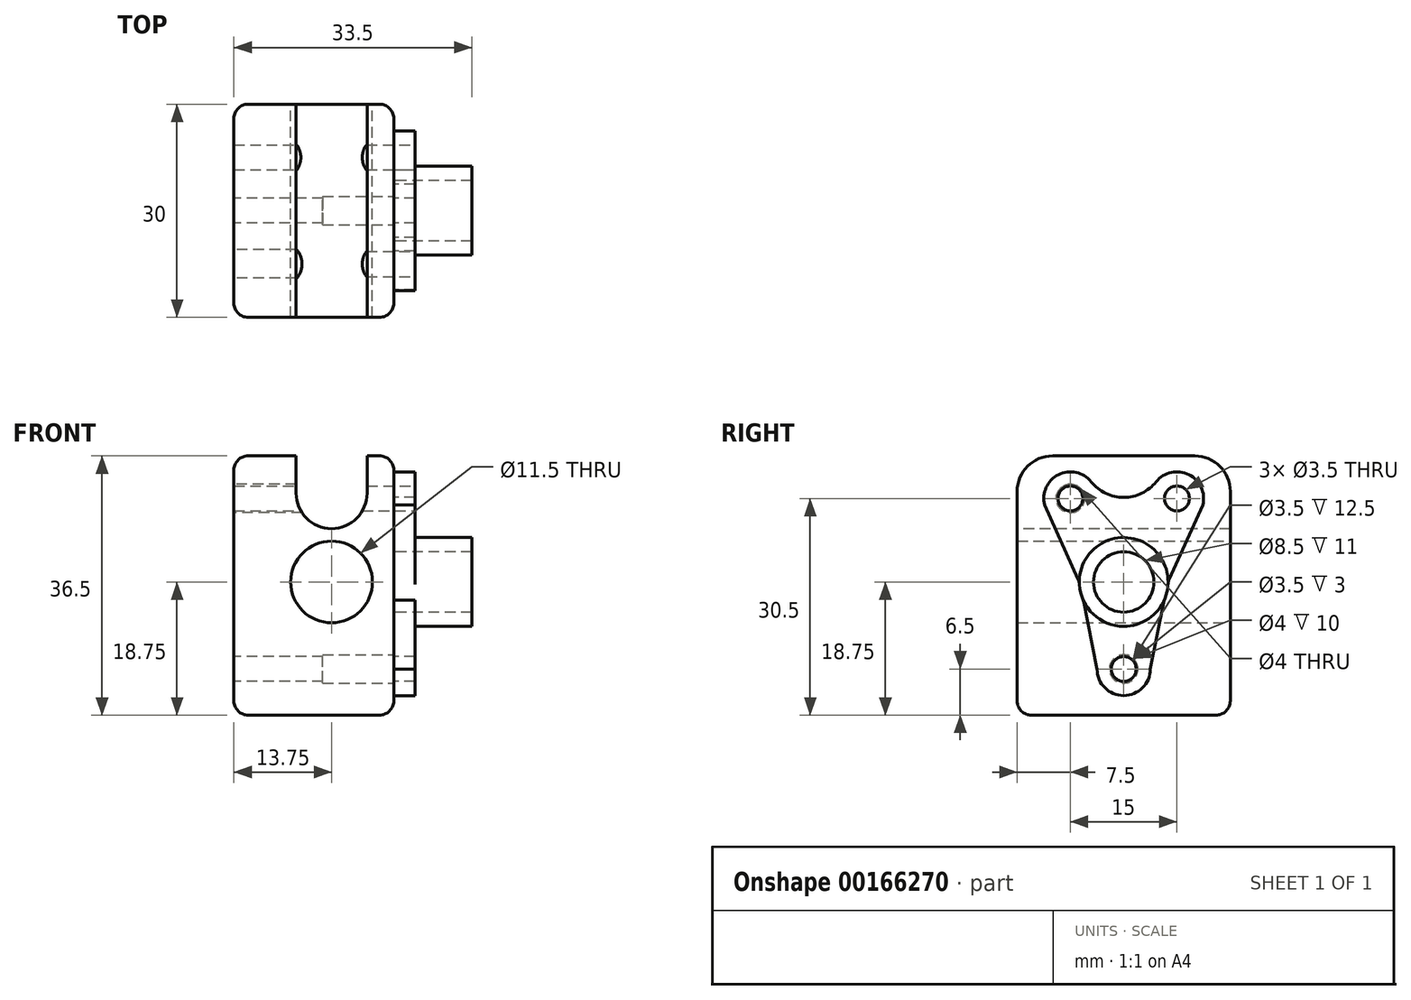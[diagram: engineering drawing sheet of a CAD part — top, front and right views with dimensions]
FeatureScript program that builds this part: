
annotation { "Feature Type Name" : "Feature", "Feature Type Description" : "" }
export const myFeature = defineFeature(function(context is Context, id is Id, definition is map)
    precondition{}
    {
        {
            var Q0;
            Q0=qCreatedBy(makeId("Front.planeOp"),FACE);
            var sketch = newSketch(context, id + "F0", { "sketchPlane" : qUnion([Q0])});
            skCircle(sketch, "E0", {"center": v(0, 0) * mm, "radius": 5.75 * mm});
            skLineSegment(sketch, "E1.bottom", {"start": v(-13.75, 17.75) * mm, "end": v(8.75, 17.75) * mm});
            skLineSegment(sketch, "E1.left", {"start": v(-13.75, 17.75) * mm, "end": v(-13.75, -8.75) * mm});
            skLineSegment(sketch, "E1.right", {"start": v(8.75, 17.75) * mm, "end": v(8.75, -8.75) * mm});
            skLineSegment(sketch, "E2", {"start": v(0, 0) * mm, "end": v(0, 17.75) * mm, "construction": true});
            skLineSegment(sketch, "E3", {"start": v(8.75, -8.75) * mm, "end": v(-5.75, -8.75) * mm});
            skLineSegment(sketch, "E4", {"start": v(-13.75, -16) * mm, "end": v(-5.75, -16) * mm, "construction": true});
            skLineSegment(sketch, "E5", {"start": v(-13.75, -16) * mm, "end": v(-13.75, -23.25) * mm, "construction": true});
            skLineSegment(sketch, "E6", {"start": v(-13.75, -23.25) * mm, "end": v(-5.75, -23.25) * mm, "construction": true});
            skLineSegment(sketch, "E7", {"start": v(-5.75, -23.25) * mm, "end": v(-5.75, -16) * mm, "construction": true});
            skLineSegment(sketch, "E8", {"start": v(-5.75, -16) * mm, "end": v(-5.75, -8.75) * mm, "construction": true});
            skCircle(sketch, "E9", {"center": v(-5.75, -16) * mm, "radius": 2.5 * mm, "construction": true});
            skLineSegment(sketch, "E10", {"start": v(-5.75, -8.75) * mm, "end": v(-5.75, 0) * mm, "construction": true});
            skLineSegment(sketch, "E11", {"start": v(-5.75, -23.25) * mm, "end": v(8.75, -23.25) * mm, "construction": true});
            skLineSegment(sketch, "E12", {"start": v(8.75, -23.25) * mm, "end": v(8.75, -8.75) * mm, "construction": true});
            skLineSegment(sketch, "E13", {"start": v(-5.75, -8.75) * mm, "end": v(-13.75, -8.75) * mm});
            skSolve(sketch);
        }
        {
            var Q0;
            Q0=qSketchRegion(id+"F0",true);
            extrude(context, id + "F1", {"entities" : qUnion([Q0]), "depth" : 30 * mm});
        }
        {
            var Q0;
            {var subQ0=sQuery(id+"F0.wireOp",EDGE,"E1.right");Q0=makeQuery(id+"FleU8CKk3SzImxh_1.boolean.opBoolean","MERGE",FACE,{"derivedFrom":[makeQuery(id+"F1.opExtrude","SWEPT_FACE",FACE,{"disambiguationData":[OSD([subQ0])]}),makeQuery(id+"FleU8CKk3SzImxh_1.opExtrude","CAP_FACE",FACE,{"disambiguationData":[OSD([subQ0])],"isStart":false})]});}
            var sketch = newSketch(context, id + "F2", { "sketchPlane" : qUnion([Q0])});
            skLineSegment(sketch, "E14", {"start": v(0, -5.75) * mm, "end": v(-30, -5.75) * mm, "construction": true});
            skLineSegment(sketch, "E15", {"start": v(-30, 5.75) * mm, "end": v(0, 5.75) * mm, "construction": true});
            skLineSegment(sketch, "E16", {"start": v(-15, -5.75) * mm, "end": v(-15, 5.75) * mm, "construction": true});
            skCircle(sketch, "E17", {"center": v(-15, 0) * mm, "radius": 4.25 * mm});
            skArc(sketch, "E18.0", {"start": v(-21.25, 0) * mm, "mid": v(-15, -6.25) * mm, "end": v(-8.75, 0) * mm});
            skLineSegment(sketch, "E19", {"start": v(-15, 5.75) * mm, "end": v(-15, 17.75) * mm, "construction": true});
            skCircle(sketch, "E20", {"center": v(-22.5, 11.75) * mm, "radius": 1.75 * mm});
            skPoint(sketch, "E20.centerSnap0", {"position": v(-15, 11.75) * mm});
            skCircle(sketch, "E21.MirrorC", {"center": v(-7.5, 11.75) * mm, "radius": 1.75 * mm});
            skLineSegment(sketch, "E22", {"start": v(-30, 17.75) * mm, "end": v(-15, 17.75) * mm, "construction": true});
            skPoint(sketch, "E23", {"position": v(-22.5, 17.75) * mm});
            skArc(sketch, "E24.0", {"start": v(-19.57, 14.1) * mm, "mid": v(-24.72, 14.77) * mm, "end": v(-25.6, 9.65) * mm});
            skArc(sketch, "E25.MirrorC", {"start": v(-10.43, 14.1) * mm, "mid": v(-5.82, 15.1) * mm, "end": v(-3.87, 10.81) * mm});
            skLineSegment(sketch, "E26", {"start": v(-3.87, 10.81) * mm, "end": v(-8.75, 0) * mm});
            skArc(sketch, "E27", {"start": v(-19.57, 14.1) * mm, "mid": v(-15, 11.9) * mm, "end": v(-10.43, 14.1) * mm});
            skLineSegment(sketch, "E28.MirrorCS", {"start": v(-26.13, 10.81) * mm, "end": v(-21.25, 0) * mm});
            skSolve(sketch);
        }
        {
            var Q0;
            Q0=makeQuery(id+"F2.imprint","IMPRINT",FACE,{"disambiguationData":[TD([[makeQuery(id+"F2.imprint","IMPRINT",EDGE,{"derivedFrom":sQuery(id+"F2.wireOp",EDGE,"E17")}),-1.0]])]});
            extrude(context, id + "F3", {"entities" : qUnion([Q0]), "depth" : 3 * mm});
        }
        {
            var Q0;
            Q0=makeQuery(id+"F3.opExtrude","CAP_FACE",FACE,{"disambiguationData":[OSD([sQuery(id+"F2.wireOp",EDGE,"E17"),sQuery(id+"F2.wireOp",EDGE,"E18.0"),sQuery(id+"F2.wireOp",EDGE,"E20"),sQuery(id+"F2.wireOp",EDGE,"E21.MirrorC"),sQuery(id+"F2.wireOp",EDGE,"E24.0"),sQuery(id+"F2.wireOp",EDGE,"E25.MirrorC"),sQuery(id+"F2.wireOp",EDGE,"E26"),sQuery(id+"F2.wireOp",EDGE,"E27"),sQuery(id+"F2.wireOp",EDGE,"E28.MirrorCS")])],"isStart":false});
            var sketch = newSketch(context, id + "F4", { "sketchPlane" : qUnion([Q0])});
            skCircle(sketch, "E29.0", {"center": v(-15, 0) * mm, "radius": 4.25 * mm});
            skCircle(sketch, "E30", {"center": v(-15, 0) * mm, "radius": 6.25 * mm});
            skSolve(sketch);
        }
        {
            var Q0;
            Q0=makeQuery(id+"F4.imprint","IMPRINT",FACE,{"disambiguationData":[TD([[makeQuery(id+"F4.imprint","IMPRINT",EDGE,{"derivedFrom":sQuery(id+"F4.wireOp",EDGE,"E29.0")}),-1.0]])]});
            extrude(context, id + "F5", {"entities" : qUnion([Q0]), "operationType" : NewBodyOperationType.ADD, "depth" : 8 * mm});
        }
        {
            var Q0;
            {var subQ0=sQuery(id+"F0.wireOp",EDGE,"E1.right");Q0=makeQuery(id+"FleU8CKk3SzImxh_1.boolean.opBoolean","MERGE",FACE,{"derivedFrom":[makeQuery(id+"F1.opExtrude","SWEPT_FACE",FACE,{"disambiguationData":[OSD([subQ0])]}),makeQuery(id+"FleU8CKk3SzImxh_1.opExtrude","CAP_FACE",FACE,{"disambiguationData":[OSD([subQ0])],"isStart":false})]});}
            var sketch = newSketch(context, id + "F6", { "sketchPlane" : qUnion([Q0])});
            skCircle(sketch, "E31.0", {"center": v(-22.5, 11.75) * mm, "radius": 1.75 * mm});
            skCircle(sketch, "E32.0", {"center": v(-7.5, 11.75) * mm, "radius": 1.75 * mm});
            skSolve(sketch);
        }
        {
            var Q0;
            Q0=makeQuery(id+"F6.imprint","IMPRINT",FACE,{"disambiguationData":[TD([[makeQuery(id+"F6.imprint","IMPRINT",EDGE,{"derivedFrom":sQuery(id+"F6.wireOp",EDGE,"E31.0")}),1.0]])]});
            var Q1;
            Q1=makeQuery(id+"F6.imprint","IMPRINT",FACE,{"disambiguationData":[TD([[makeQuery(id+"F6.imprint","IMPRINT",EDGE,{"derivedFrom":sQuery(id+"F6.wireOp",EDGE,"E32.0")}),1.0]])]});
            extrude(context, id + "F7", {"entities" : qUnion([Q0, Q1]), "operationType" : NewBodyOperationType.REMOVE, "endBound" : BoundingType.THROUGH_ALL, "oppositeDirection" : true, "depth" : 25 * mm});
        }
        {
            var Q0;
            Q0=makeQuery(id+"F1.opExtrude","CAP_FACE",FACE,{"disambiguationData":[OSD([sQuery(id+"F0.wireOp",EDGE,"E0"),sQuery(id+"F0.wireOp",EDGE,"E1.bottom"),sQuery(id+"F0.wireOp",EDGE,"E1.left"),sQuery(id+"F0.wireOp",EDGE,"E1.right"),sQuery(id+"F0.wireOp",EDGE,"E5"),sQuery(id+"F0.wireOp",EDGE,"E6"),sQuery(id+"F0.wireOp",EDGE,"E11"),sQuery(id+"F0.wireOp",EDGE,"E12")])],"isStart":true});
            var sketch = newSketch(context, id + "F8", { "sketchPlane" : qUnion([Q0])});
            skLineSegment(sketch, "E33", {"start": v(-8.57, 13.5) * mm, "end": v(11.58, 13.5) * mm, "construction": true});
            skLineSegment(sketch, "E34", {"start": v(11.58, 10) * mm, "end": v(-8.57, 10) * mm, "construction": true});
            skCircle(sketch, "E35.0", {"center": v(0, 0) * mm, "radius": 5.75 * mm, "construction": true});
            skLineSegment(sketch, "E36", {"start": v(0, 0) * mm, "end": v(0, 17.75) * mm, "construction": true});
            skLineSegment(sketch, "E37", {"start": v(5, 10) * mm, "end": v(5, 13.5) * mm, "construction": true});
            skLineSegment(sketch, "E38", {"start": v(0, 7.5) * mm, "end": v(5, 7.5) * mm});
            skLineSegment(sketch, "E39", {"start": v(5, 7.5) * mm, "end": v(5, 17.75) * mm});
            skLineSegment(sketch, "E40.MirrorCS", {"start": v(0, 7.5) * mm, "end": v(-5, 7.5) * mm});
            skLineSegment(sketch, "E41.MirrorCS", {"start": v(-5, 7.5) * mm, "end": v(-5, 17.75) * mm});
            skLineSegment(sketch, "E42", {"start": v(-5, 17.75) * mm, "end": v(5, 17.75) * mm});
            skSolve(sketch);
        }
        {
            var Q0;
            Q0=makeQuery(id+"F8.imprint","IMPRINT",FACE,{"disambiguationData":[TD([[makeQuery(id+"F8.imprint","IMPRINT",EDGE,{"derivedFrom":sQuery(id+"F8.wireOp",EDGE,"E38")}),1.0]])]});
            extrude(context, id + "F9", {"entities" : qUnion([Q0]), "operationType" : NewBodyOperationType.REMOVE, "endBound" : BoundingType.THROUGH_ALL, "oppositeDirection" : true, "depth" : 25 * mm});
        }
        {
            var Q0;
            {var subQ1=sQuery(id+"F0.wireOp",EDGE,"E1.bottom");Q0=makeQuery(id+"F9.boolean.opBoolean","SPLIT",EDGE,{"disambiguationData":[TD([makeQuery(id+"F9.opExtrude","SWEPT_FACE",FACE,{"disambiguationData":[OSD([sQuery(id+"F8.wireOp",EDGE,"E39")])]})])],"derivedFrom":makeQuery(id+"F1.opExtrude","CAP_EDGE",EDGE,{"disambiguationData":[OSD([subQ1])],"isStart":true})});}
            var Q1;
            {var subQ2=sQuery(id+"F0.wireOp",EDGE,"E1.bottom");Q1=makeQuery(id+"F9.boolean.opBoolean","SPLIT",EDGE,{"disambiguationData":[TD([makeQuery(id+"F9.opExtrude","SWEPT_FACE",FACE,{"disambiguationData":[OSD([sQuery(id+"F8.wireOp",EDGE,"E41.MirrorCS")])]})])],"derivedFrom":makeQuery(id+"F1.opExtrude","CAP_EDGE",EDGE,{"disambiguationData":[OSD([subQ2])],"isStart":true})});}
            var Q2;
            Q2=makeQuery(id+"F9.boolean.opBoolean","COPY",EDGE,{"derivedFrom":makeQuery(id+"F9.opExtrude","SWEPT_EDGE",EDGE,{"disambiguationData":[OSD([sQuery(id+"F8.wireOp",EDGE,"E38"),sQuery(id+"F8.wireOp",EDGE,"E39")])]})});
            var Q3;
            {var subQ2=sQuery(id+"F0.wireOp",EDGE,"E1.bottom");Q3=makeQuery(id+"F9.boolean.opBoolean","SPLIT",EDGE,{"disambiguationData":[TD([makeQuery(id+"F9.opExtrude","SWEPT_FACE",FACE,{"disambiguationData":[OSD([sQuery(id+"F8.wireOp",EDGE,"E39")])]})])],"derivedFrom":makeQuery(id+"F1.opExtrude","CAP_EDGE",EDGE,{"disambiguationData":[OSD([subQ2])],"isStart":false})});}
            var Q4;
            Q4=makeQuery(id+"F9.boolean.opBoolean","COPY",EDGE,{"derivedFrom":makeQuery(id+"F9.opExtrude","SWEPT_EDGE",EDGE,{"disambiguationData":[OSD([sQuery(id+"F8.wireOp",EDGE,"E40.MirrorCS"),sQuery(id+"F8.wireOp",EDGE,"E41.MirrorCS")])]})});
            var Q5;
            {var subQ1=sQuery(id+"F0.wireOp",EDGE,"E1.bottom");Q5=makeQuery(id+"F9.boolean.opBoolean","SPLIT",EDGE,{"disambiguationData":[TD([makeQuery(id+"F9.opExtrude","SWEPT_FACE",FACE,{"disambiguationData":[OSD([sQuery(id+"F8.wireOp",EDGE,"E41.MirrorCS")])]})])],"derivedFrom":makeQuery(id+"F1.opExtrude","CAP_EDGE",EDGE,{"disambiguationData":[OSD([subQ1])],"isStart":false})});}
            fillet(context, id + "F10", {"entities" : qUnion([Q0, Q1, Q2, Q3, Q4, Q5]), "radius" : 5 * mm, "tangentPropagation" : true, "allowEdgeOverflow" : false});
        }
        {
            var Q0;
            Q0=makeQuery(id+"F3.opExtrude","CAP_FACE",FACE,{"disambiguationData":[OSD([sQuery(id+"F2.wireOp",EDGE,"E17"),sQuery(id+"F2.wireOp",EDGE,"E18.0"),sQuery(id+"F2.wireOp",EDGE,"E20"),sQuery(id+"F2.wireOp",EDGE,"E21.MirrorC"),sQuery(id+"F2.wireOp",EDGE,"E24.0"),sQuery(id+"F2.wireOp",EDGE,"E25.MirrorC"),sQuery(id+"F2.wireOp",EDGE,"E26"),sQuery(id+"F2.wireOp",EDGE,"E27"),sQuery(id+"F2.wireOp",EDGE,"E28.MirrorCS")])],"isStart":true});
            var sketch = newSketch(context, id + "F11", { "sketchPlane" : qUnion([Q0])});
            skCircle(sketch, "E43.0", {"center": v(15, 0) * mm, "radius": 4.25 * mm});
            skLineSegment(sketch, "E44", {"start": v(15, 0) * mm, "end": v(15, -12.25) * mm, "construction": true});
            skCircle(sketch, "E45", {"center": v(15, -12.25) * mm, "radius": 1.75 * mm});
            skCircle(sketch, "E46.0", {"center": v(15, -12.25) * mm, "radius": 3.75 * mm});
            skLineSegment(sketch, "E47", {"start": v(11.25, -12.25) * mm, "end": v(9.3, -2.58) * mm});
            skLineSegment(sketch, "E48.MirrorCS", {"start": v(18.75, -12.25) * mm, "end": v(20.7, -2.58) * mm});
            skSolve(sketch);
        }
        {
            var Q0;
            {var subQ0=sQuery(id+"F11.wireOp",EDGE,"E47");Q0=makeQuery(id+"F11.imprint","IMPRINT",FACE,{"disambiguationData":[TD([[makeQuery(id+"F11.imprint","IMPRINT",EDGE,{"derivedFrom":subQ0}),-1.0]])]});}
            var Q1;
            Q1=makeQuery(id+"F11.imprint","IMPRINT",FACE,{"disambiguationData":[TD([[makeQuery(id+"F11.imprint","IMPRINT",EDGE,{"derivedFrom":sQuery(id+"F11.wireOp",EDGE,"E45")}),-1.0]])]});
            var Q2;
            Q2=makeQuery(id+"F3.opExtrude","CAP_FACE",FACE,{"disambiguationData":[OSD([sQuery(id+"F2.wireOp",EDGE,"E17"),sQuery(id+"F2.wireOp",EDGE,"E18.0"),sQuery(id+"F2.wireOp",EDGE,"E20"),sQuery(id+"F2.wireOp",EDGE,"E21.MirrorC"),sQuery(id+"F2.wireOp",EDGE,"E24.0"),sQuery(id+"F2.wireOp",EDGE,"E25.MirrorC"),sQuery(id+"F2.wireOp",EDGE,"E26"),sQuery(id+"F2.wireOp",EDGE,"E27"),sQuery(id+"F2.wireOp",EDGE,"E28.MirrorCS")])],"isStart":false});
            extrude(context, id + "F12", {"entities" : qUnion([Q0, Q1]), "operationType" : NewBodyOperationType.ADD, "endBound" : BoundingType.UP_TO_SURFACE, "oppositeDirection" : true, "endBoundEntityFace" : qUnion([Q2]), "depth" : 25 * mm});
        }
        {
            var Q0;
            Q0=makeQuery(id+"F1.opExtrude","SWEPT_FACE",FACE,{"disambiguationData":[OSD([sQuery(id+"F0.wireOp",EDGE,"E3"),sQuery(id+"F0.wireOp",EDGE,"E13")])]});
            extrude(context, id + "F13", {"entities" : qUnion([Q0]), "operationType" : NewBodyOperationType.ADD, "depth" : 10 * mm});
        }
        {
            var Q0;
            Q0=makeQuery(id+"F1.opExtrude","SWEPT_EDGE",EDGE,{"disambiguationData":[OSD([sQuery(id+"F0.wireOp",EDGE,"E1.bottom"),sQuery(id+"F0.wireOp",EDGE,"E1.right")])]});
            var Q1;
            Q1=makeQuery(id+"F1.opExtrude","CAP_EDGE",EDGE,{"disambiguationData":[OSD([sQuery(id+"F0.wireOp",EDGE,"E1.right"),sQuery(id+"F0.wireOp",EDGE,"E12")])],"isStart":false});
            var Q2;
            Q2=makeQuery(id+"F1.opExtrude","CAP_EDGE",EDGE,{"disambiguationData":[OSD([sQuery(id+"F0.wireOp",EDGE,"E1.right"),sQuery(id+"F0.wireOp",EDGE,"E12")])],"isStart":true});
            var Q3;
            Q3=makeQuery(id+"F5.opExtrude","CAP_EDGE",EDGE,{"disambiguationData":[OSD([sQuery(id+"F4.wireOp",EDGE,"E30")])],"isStart":true});
            var Q4;
            Q4=makeQuery(id+"F3.opExtrude","SWEPT_EDGE",EDGE,{"disambiguationData":[OSD([sQuery(id+"F2.wireOp",EDGE,"E18.0"),sQuery(id+"F2.wireOp",EDGE,"E28.MirrorCS")])]});
            var Q5;
            Q5=makeQuery(id+"F3.opExtrude","SWEPT_EDGE",EDGE,{"disambiguationData":[OSD([sQuery(id+"F2.wireOp",EDGE,"E18.0"),sQuery(id+"F2.wireOp",EDGE,"E26")])]});
            var Q6;
            Q6=makeQuery(id+"F1.opExtrude","SWEPT_EDGE",EDGE,{"disambiguationData":[OSD([sQuery(id+"F0.wireOp",EDGE,"E5"),sQuery(id+"F0.wireOp",EDGE,"E6")])]});
            var Q7;
            Q7=makeQuery(id+"F1.opExtrude","CAP_EDGE",EDGE,{"disambiguationData":[OSD([sQuery(id+"F0.wireOp",EDGE,"E6"),sQuery(id+"F0.wireOp",EDGE,"E11")])],"isStart":false});
            var Q8;
            Q8=makeQuery(id+"F1.opExtrude","CAP_EDGE",EDGE,{"disambiguationData":[OSD([sQuery(id+"F0.wireOp",EDGE,"E6"),sQuery(id+"F0.wireOp",EDGE,"E11")])],"isStart":true});
            var Q9;
            Q9=makeQuery(id+"F1.opExtrude","CAP_EDGE",EDGE,{"disambiguationData":[OSD([sQuery(id+"F0.wireOp",EDGE,"E1.left"),sQuery(id+"F0.wireOp",EDGE,"E5")])],"isStart":false});
            var Q10;
            Q10=makeQuery(id+"F1.opExtrude","SWEPT_EDGE",EDGE,{"disambiguationData":[OSD([sQuery(id+"F0.wireOp",EDGE,"E1.bottom"),sQuery(id+"F0.wireOp",EDGE,"E1.left")])]});
            var Q11;
            Q11=makeQuery(id+"F1.opExtrude","CAP_EDGE",EDGE,{"disambiguationData":[OSD([sQuery(id+"F0.wireOp",EDGE,"E1.left")])],"isStart":true});
            var Q12;
            {var subQ0=sQuery(id+"F0.wireOp",EDGE,"E13");var subQ1=sQuery(id+"F0.wireOp",EDGE,"E3");Q12=makeQuery(id+"F13.opExtrude","CAP_EDGE",EDGE,{"disambiguationData":[OSD([subQ1,subQ0]),TDD([makeQuery(id+"F1.opExtrude","CAP_EDGE",EDGE,{"disambiguationData":[OSD([subQ1,subQ0])],"isStart":false})])],"isStart":false});}
            var Q13;
            {var subQ0=sQuery(id+"F0.wireOp",EDGE,"E13");var subQ1=sQuery(id+"F0.wireOp",EDGE,"E3");Q13=makeQuery(id+"F13.opExtrude","CAP_EDGE",EDGE,{"disambiguationData":[OSD([subQ1,subQ0]),TDD([makeQuery(id+"F1.opExtrude","CAP_EDGE",EDGE,{"disambiguationData":[OSD([subQ1,subQ0])],"isStart":true})])],"isStart":false});}
            var Q14;
            Q14=makeQuery(id+"F13.opExtrude","CAP_EDGE",EDGE,{"disambiguationData":[OSD([sQuery(id+"F0.wireOp",EDGE,"E1.left"),sQuery(id+"F0.wireOp",EDGE,"E13")])],"isStart":false});
            var Q15;
            Q15=makeQuery(id+"F13.opExtrude","CAP_EDGE",EDGE,{"disambiguationData":[OSD([sQuery(id+"F0.wireOp",EDGE,"E1.right"),sQuery(id+"F0.wireOp",EDGE,"E3")])],"isStart":false});
            var Q16;
            Q16=makeQuery(id+"F12.opExtrude","CAP_EDGE",EDGE,{"disambiguationData":[OSD([sQuery(id+"F2.wireOp",EDGE,"E18.0")])],"isStart":false});
            fillet(context, id + "F14", {"entities" : qUnion([Q0, Q1, Q2, Q3, Q4, Q5, Q6, Q7, Q8, Q9, Q10, Q11, Q12, Q13, Q14, Q15, Q16]), "radius" : 2 * mm, "tangentPropagation" : true, "allowEdgeOverflow" : false});
        }
        {
            var Q0;
            {var subQ0=sQuery(id+"F0.wireOp",EDGE,"E1.right");Q0=makeQuery(id+"F13.boolean.opBoolean","MERGE",FACE,{"derivedFrom":[makeQuery(id+"F1.opExtrude","SWEPT_FACE",FACE,{"disambiguationData":[OSD([subQ0])]}),makeQuery(id+"F13.opExtrude","SWEPT_FACE",FACE,{"disambiguationData":[OSD([subQ0,sQuery(id+"F0.wireOp",EDGE,"E3")])]})]});}
            var sketch = newSketch(context, id + "F15", { "sketchPlane" : qUnion([Q0])});
            skCircle(sketch, "E49.0", {"center": v(-15, -12.25) * mm, "radius": 1.75 * mm});
            skSolve(sketch);
        }
        {
            var Q0;
            Q0=makeQuery(id+"F15.imprint","IMPRINT",FACE,{"disambiguationData":[TD([[makeQuery(id+"F15.imprint","IMPRINT",EDGE,{"derivedFrom":sQuery(id+"F15.wireOp",EDGE,"E49.0")}),1.0]])]});
            extrude(context, id + "F16", {"entities" : qUnion([Q0]), "operationType" : NewBodyOperationType.REMOVE, "endBound" : BoundingType.THROUGH_ALL, "oppositeDirection" : true, "depth" : 25 * mm});
        }
        {
            var Q0;
            {var subQ0=sQuery(id+"F0.wireOp",EDGE,"E1.right");Q0=makeQuery(id+"F13.boolean.opBoolean","MERGE",FACE,{"derivedFrom":[makeQuery(id+"F1.opExtrude","SWEPT_FACE",FACE,{"disambiguationData":[OSD([subQ0])]}),makeQuery(id+"F13.opExtrude","SWEPT_FACE",FACE,{"disambiguationData":[OSD([subQ0,sQuery(id+"F0.wireOp",EDGE,"E3")])]})]});}
            var sketch = newSketch(context, id + "F17", { "sketchPlane" : qUnion([Q0])});
            skCircle(sketch, "E50.0", {"center": v(-15, -12.25) * mm, "radius": 1.75 * mm});
            skCircle(sketch, "E51.0", {"center": v(-15, -12.25) * mm, "radius": 1.8 * mm});
            skSolve(sketch);
        }
        {
            var Q0;
            Q0=makeQuery(id+"F17.imprint","IMPRINT",FACE,{"disambiguationData":[TD([[makeQuery(id+"F17.imprint","IMPRINT",EDGE,{"derivedFrom":sQuery(id+"F17.wireOp",EDGE,"E50.0")}),1.0]])]});
            extrude(context, id + "F18", {"entities" : qUnion([Q0]), "operationType" : NewBodyOperationType.REMOVE, "endBound" : BoundingType.THROUGH_ALL, "oppositeDirection" : true, "depth" : 25 * mm});
        }
        {
            var Q0;
            {var subQ0=sQuery(id+"F0.wireOp",EDGE,"E1.right");Q0=makeQuery(id+"F13.boolean.opBoolean","MERGE",FACE,{"derivedFrom":[makeQuery(id+"F1.opExtrude","SWEPT_FACE",FACE,{"disambiguationData":[OSD([subQ0])]}),makeQuery(id+"F13.opExtrude","SWEPT_FACE",FACE,{"disambiguationData":[OSD([subQ0,sQuery(id+"F0.wireOp",EDGE,"E3")])]})]});}
            var sketch = newSketch(context, id + "F19", { "sketchPlane" : qUnion([Q0])});
            skCircle(sketch, "E52.0", {"center": v(-15, -12.25) * mm, "radius": 1.75 * mm, "construction": true});
            skCircle(sketch, "E53", {"center": v(-15, -12.25) * mm, "radius": 2 * mm});
            skSolve(sketch);
        }
        {
            var Q0;
            Q0=makeQuery(id+"F19.imprint","IMPRINT",FACE,{"disambiguationData":[TD([[makeQuery(id+"F19.imprint","IMPRINT",EDGE,{"derivedFrom":sQuery(id+"F19.wireOp",EDGE,"E53")}),1.0]])]});
            extrude(context, id + "F20", {"entities" : qUnion([Q0]), "operationType" : NewBodyOperationType.REMOVE, "oppositeDirection" : true, "depth" : 10 * mm});
        }
        {
            var Q0;
            {var subQ0=sQuery(id+"F0.wireOp",EDGE,"E1.left");Q0=makeQuery(id+"F13.boolean.opBoolean","MERGE",FACE,{"derivedFrom":[makeQuery(id+"F1.opExtrude","SWEPT_FACE",FACE,{"disambiguationData":[OSD([subQ0])]}),makeQuery(id+"F13.opExtrude","SWEPT_FACE",FACE,{"disambiguationData":[OSD([subQ0,sQuery(id+"F0.wireOp",EDGE,"E13")])]})]});}
            var sketch = newSketch(context, id + "F21", { "sketchPlane" : qUnion([Q0])});
            skCircle(sketch, "E54.0", {"center": v(7.5, 11.75) * mm, "radius": 1.75 * mm, "construction": true});
            skCircle(sketch, "E55.0", {"center": v(22.5, 11.75) * mm, "radius": 1.75 * mm, "construction": true});
            skCircle(sketch, "E56", {"center": v(7.5, 11.75) * mm, "radius": 2 * mm});
            skCircle(sketch, "E57", {"center": v(22.5, 11.75) * mm, "radius": 2 * mm});
            skSolve(sketch);
        }
        {
            var Q0;
            Q0=makeQuery(id+"F21.imprint","IMPRINT",FACE,{"disambiguationData":[TD([[makeQuery(id+"F21.imprint","IMPRINT",EDGE,{"derivedFrom":makeQuery(id+"F7.boolean.opBoolean","INTERSECT",EDGE,{"derivedFrom":[makeQuery(id+"F1.opExtrude","SWEPT_FACE",FACE,{"disambiguationData":[OSD([sQuery(id+"F0.wireOp",EDGE,"E1.left")])]}),makeQuery(id+"F7.opExtrude","SWEPT_FACE",FACE,{"disambiguationData":[OSD([sQuery(id+"F6.wireOp",EDGE,"E32.0")])]})]})}),-1.0]])]});
            var Q1;
            Q1=makeQuery(id+"F21.imprint","IMPRINT",FACE,{"disambiguationData":[TD([[makeQuery(id+"F21.imprint","IMPRINT",EDGE,{"derivedFrom":sQuery(id+"F21.wireOp",EDGE,"E57")}),1.0]])]});
            extrude(context, id + "F22", {"entities" : qUnion([Q0, Q1]), "operationType" : NewBodyOperationType.REMOVE, "oppositeDirection" : true, "depth" : 12.5 * mm});
        }
    });
